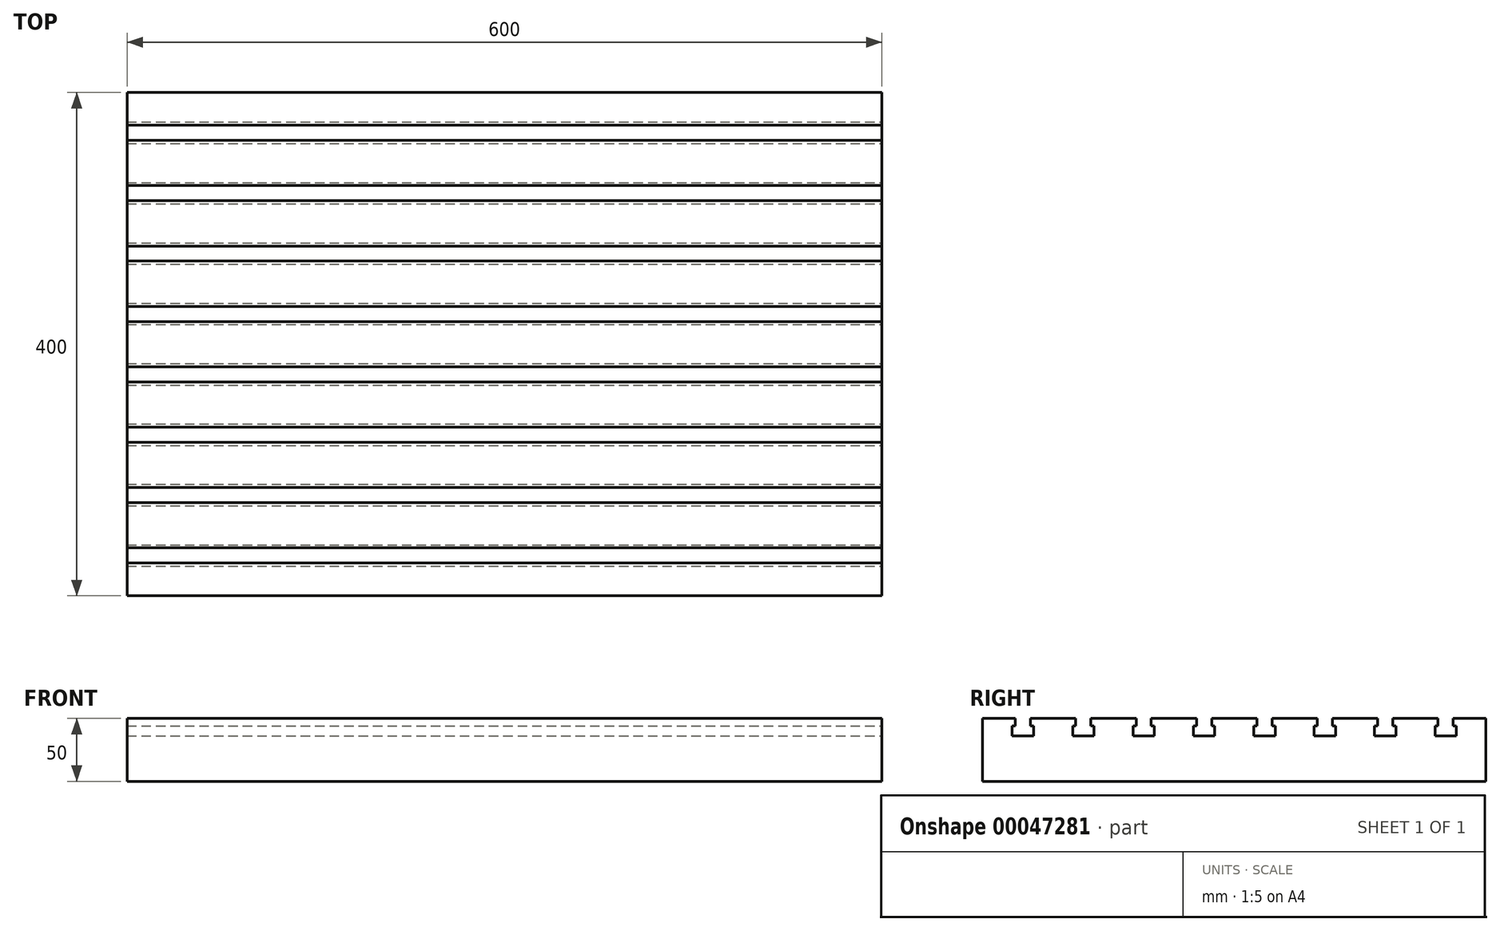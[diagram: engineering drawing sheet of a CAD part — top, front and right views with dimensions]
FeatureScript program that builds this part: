
annotation { "Feature Type Name" : "Feature", "Feature Type Description" : "" }
export const myFeature = defineFeature(function(context is Context, id is Id, definition is map)
    precondition{}
    {
        {
            var Q0;
            Q0=qCreatedBy(makeId("Right.planeOp"),FACE);
            var sketch = newSketch(context, id + "F0", { "sketchPlane" : qUnion([Q0])});
            skLineSegment(sketch, "E0.bottom", {"start": v(-200, 0) * mm, "end": v(200, 0) * mm});
            skLineSegment(sketch, "E0.top", {"start": v(-200, -50) * mm, "end": v(200, -50) * mm});
            skLineSegment(sketch, "E0.left", {"start": v(-200, 0) * mm, "end": v(-200, -50) * mm});
            skLineSegment(sketch, "E0.right", {"start": v(200, 0) * mm, "end": v(200, -50) * mm});
            skSolve(sketch);
        }
        {
            var Q0;
            Q0 = qSketchRegion(id + "F0", true);
            extrude(context, id + "F1", {"entities" : qUnion([Q0]), "endBound" : BoundingType.SYMMETRIC, "depth" : 600 * mm});
        }
        {
            var Q0;
            Q0=makeQuery(id+"F1.opExtrude","CAP_FACE",FACE,{"disambiguationData":[OSD([sQuery(id+"F0.wireOp",EDGE,"E0.bottom"),sQuery(id+"F0.wireOp",EDGE,"E0.top"),sQuery(id+"F0.wireOp",EDGE,"E0.left"),sQuery(id+"F0.wireOp",EDGE,"E0.right")])],"isStart":false});
            var sketch = newSketch(context, id + "F2", { "sketchPlane" : qUnion([Q0])});
            skLineSegment(sketch, "E1.bottom", {"start": v(-174, 0) * mm, "end": v(-162, 0) * mm});
            skLineSegment(sketch, "E1.top", {"start": v(-176.5, -6) * mm, "end": v(-174, -6) * mm});
            skLineSegment(sketch, "E1.left", {"start": v(-174, 0) * mm, "end": v(-174, -6) * mm});
            skLineSegment(sketch, "E1.right", {"start": v(-162, 0) * mm, "end": v(-162, -6) * mm});
            skLineSegment(sketch, "E2.top", {"start": v(-176.5, -14) * mm, "end": v(-159.5, -14) * mm});
            skLineSegment(sketch, "E2.left", {"start": v(-176.5, -6) * mm, "end": v(-176.5, -14) * mm});
            skLineSegment(sketch, "E2.right", {"start": v(-159.5, -6) * mm, "end": v(-159.5, -14) * mm});
            skLineSegment(sketch, "E3.trimOffspring", {"start": v(-162, -6) * mm, "end": v(-159.5, -6) * mm});
            skLineSegment(sketch, "E4", {"start": v(-168, 0) * mm, "end": v(-168, -14) * mm, "construction": true});
            skLineSegment(sketch, "E5.1.0.0", {"start": v(-120, 0) * mm, "end": v(-120, -14) * mm, "construction": true});
            skLineSegment(sketch, "E5.1.0.1", {"start": v(-128.5, -14) * mm, "end": v(-111.5, -14) * mm});
            skLineSegment(sketch, "E5.1.0.2", {"start": v(-126, 0) * mm, "end": v(-114, 0) * mm});
            skLineSegment(sketch, "E5.1.0.3", {"start": v(-111.5, -6) * mm, "end": v(-111.5, -14) * mm});
            skLineSegment(sketch, "E5.1.0.4", {"start": v(-128.5, -6) * mm, "end": v(-128.5, -14) * mm});
            skLineSegment(sketch, "E5.1.0.5", {"start": v(-114, 0) * mm, "end": v(-114, -6) * mm});
            skLineSegment(sketch, "E5.1.0.6", {"start": v(-126, 0) * mm, "end": v(-126, -6) * mm});
            skLineSegment(sketch, "E5.1.0.7", {"start": v(-128.5, -6) * mm, "end": v(-126, -6) * mm});
            skLineSegment(sketch, "E5.1.0.8", {"start": v(-114, -6) * mm, "end": v(-111.5, -6) * mm});
            skLineSegment(sketch, "E5.2.0.0", {"start": v(-72, 0) * mm, "end": v(-72, -14) * mm, "construction": true});
            skLineSegment(sketch, "E5.2.0.1", {"start": v(-80.5, -14) * mm, "end": v(-63.5, -14) * mm});
            skLineSegment(sketch, "E5.2.0.2", {"start": v(-78, 0) * mm, "end": v(-66, 0) * mm});
            skLineSegment(sketch, "E5.2.0.3", {"start": v(-63.5, -6) * mm, "end": v(-63.5, -14) * mm});
            skLineSegment(sketch, "E5.2.0.4", {"start": v(-80.5, -6) * mm, "end": v(-80.5, -14) * mm});
            skLineSegment(sketch, "E5.2.0.5", {"start": v(-66, 0) * mm, "end": v(-66, -6) * mm});
            skLineSegment(sketch, "E5.2.0.6", {"start": v(-78, 0) * mm, "end": v(-78, -6) * mm});
            skLineSegment(sketch, "E5.2.0.7", {"start": v(-80.5, -6) * mm, "end": v(-78, -6) * mm});
            skLineSegment(sketch, "E5.2.0.8", {"start": v(-66, -6) * mm, "end": v(-63.5, -6) * mm});
            skLineSegment(sketch, "E5.3.0.0", {"start": v(-24, 0) * mm, "end": v(-24, -14) * mm, "construction": true});
            skLineSegment(sketch, "E5.3.0.1", {"start": v(-32.5, -14) * mm, "end": v(-15.5, -14) * mm});
            skLineSegment(sketch, "E5.3.0.2", {"start": v(-30, 0) * mm, "end": v(-18, 0) * mm});
            skLineSegment(sketch, "E5.3.0.3", {"start": v(-15.5, -6) * mm, "end": v(-15.5, -14) * mm});
            skLineSegment(sketch, "E5.3.0.4", {"start": v(-32.5, -6) * mm, "end": v(-32.5, -14) * mm});
            skLineSegment(sketch, "E5.3.0.5", {"start": v(-18, 0) * mm, "end": v(-18, -6) * mm});
            skLineSegment(sketch, "E5.3.0.6", {"start": v(-30, 0) * mm, "end": v(-30, -6) * mm});
            skLineSegment(sketch, "E5.3.0.7", {"start": v(-32.5, -6) * mm, "end": v(-30, -6) * mm});
            skLineSegment(sketch, "E5.3.0.8", {"start": v(-18, -6) * mm, "end": v(-15.5, -6) * mm});
            skLineSegment(sketch, "E5.4.0.0", {"start": v(24, 0) * mm, "end": v(24, -14) * mm, "construction": true});
            skLineSegment(sketch, "E5.4.0.1", {"start": v(15.5, -14) * mm, "end": v(32.5, -14) * mm});
            skLineSegment(sketch, "E5.4.0.2", {"start": v(18, 0) * mm, "end": v(30, 0) * mm});
            skLineSegment(sketch, "E5.4.0.3", {"start": v(32.5, -6) * mm, "end": v(32.5, -14) * mm});
            skLineSegment(sketch, "E5.4.0.4", {"start": v(15.5, -6) * mm, "end": v(15.5, -14) * mm});
            skLineSegment(sketch, "E5.4.0.5", {"start": v(30, 0) * mm, "end": v(30, -6) * mm});
            skLineSegment(sketch, "E5.4.0.6", {"start": v(18, 0) * mm, "end": v(18, -6) * mm});
            skLineSegment(sketch, "E5.4.0.7", {"start": v(15.5, -6) * mm, "end": v(18, -6) * mm});
            skLineSegment(sketch, "E5.4.0.8", {"start": v(30, -6) * mm, "end": v(32.5, -6) * mm});
            skLineSegment(sketch, "E5.5.0.0", {"start": v(72, 0) * mm, "end": v(72, -14) * mm, "construction": true});
            skLineSegment(sketch, "E5.5.0.1", {"start": v(63.5, -14) * mm, "end": v(80.5, -14) * mm});
            skLineSegment(sketch, "E5.5.0.2", {"start": v(66, 0) * mm, "end": v(78, 0) * mm});
            skLineSegment(sketch, "E5.5.0.3", {"start": v(80.5, -6) * mm, "end": v(80.5, -14) * mm});
            skLineSegment(sketch, "E5.5.0.4", {"start": v(63.5, -6) * mm, "end": v(63.5, -14) * mm});
            skLineSegment(sketch, "E5.5.0.5", {"start": v(78, 0) * mm, "end": v(78, -6) * mm});
            skLineSegment(sketch, "E5.5.0.6", {"start": v(66, 0) * mm, "end": v(66, -6) * mm});
            skLineSegment(sketch, "E5.5.0.7", {"start": v(63.5, -6) * mm, "end": v(66, -6) * mm});
            skLineSegment(sketch, "E5.5.0.8", {"start": v(78, -6) * mm, "end": v(80.5, -6) * mm});
            skLineSegment(sketch, "E5.6.0.0", {"start": v(120, 0) * mm, "end": v(120, -14) * mm, "construction": true});
            skLineSegment(sketch, "E5.6.0.1", {"start": v(111.5, -14) * mm, "end": v(128.5, -14) * mm});
            skLineSegment(sketch, "E5.6.0.2", {"start": v(114, 0) * mm, "end": v(126, 0) * mm});
            skLineSegment(sketch, "E5.6.0.3", {"start": v(128.5, -6) * mm, "end": v(128.5, -14) * mm});
            skLineSegment(sketch, "E5.6.0.4", {"start": v(111.5, -6) * mm, "end": v(111.5, -14) * mm});
            skLineSegment(sketch, "E5.6.0.5", {"start": v(126, 0) * mm, "end": v(126, -6) * mm});
            skLineSegment(sketch, "E5.6.0.6", {"start": v(114, 0) * mm, "end": v(114, -6) * mm});
            skLineSegment(sketch, "E5.6.0.7", {"start": v(111.5, -6) * mm, "end": v(114, -6) * mm});
            skLineSegment(sketch, "E5.6.0.8", {"start": v(126, -6) * mm, "end": v(128.5, -6) * mm});
            skLineSegment(sketch, "E5.7.0.0", {"start": v(168, 0) * mm, "end": v(168, -14) * mm, "construction": true});
            skLineSegment(sketch, "E5.7.0.1", {"start": v(159.5, -14) * mm, "end": v(176.5, -14) * mm});
            skLineSegment(sketch, "E5.7.0.2", {"start": v(162, 0) * mm, "end": v(174, 0) * mm});
            skLineSegment(sketch, "E5.7.0.3", {"start": v(176.5, -6) * mm, "end": v(176.5, -14) * mm});
            skLineSegment(sketch, "E5.7.0.4", {"start": v(159.5, -6) * mm, "end": v(159.5, -14) * mm});
            skLineSegment(sketch, "E5.7.0.5", {"start": v(174, 0) * mm, "end": v(174, -6) * mm});
            skLineSegment(sketch, "E5.7.0.6", {"start": v(162, 0) * mm, "end": v(162, -6) * mm});
            skLineSegment(sketch, "E5.7.0.7", {"start": v(159.5, -6) * mm, "end": v(162, -6) * mm});
            skLineSegment(sketch, "E5.7.0.8", {"start": v(174, -6) * mm, "end": v(176.5, -6) * mm});
            skLineSegment(sketch, "E5.direction1", {"start": v(-168, -14) * mm, "end": v(-120, -14) * mm, "construction": true});
            skLineSegment(sketch, "E6", {"start": v(0, 0) * mm, "end": v(0, 59.23) * mm, "construction": true});
            skPoint(sketch, "E6.endSnap0", {"position": v(0, 0) * mm});
            skSolve(sketch);
        }
        {
            var Q0;
            Q0 = qSketchRegion(id + "F2", true);
            extrude(context, id + "F3", {"entities" : qUnion([Q0]), "operationType" : NewBodyOperationType.REMOVE, "endBound" : BoundingType.THROUGH_ALL, "oppositeDirection" : true, "depth" : 25 * mm});
        }
    });
